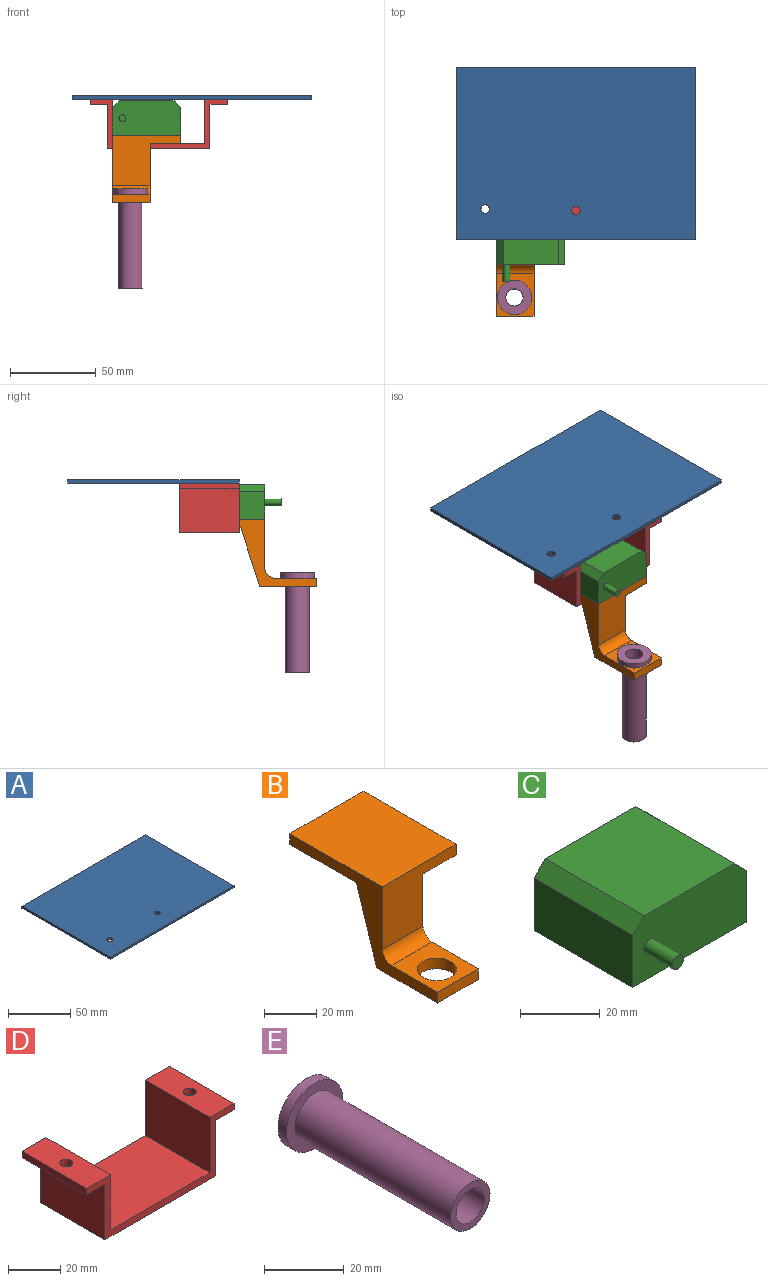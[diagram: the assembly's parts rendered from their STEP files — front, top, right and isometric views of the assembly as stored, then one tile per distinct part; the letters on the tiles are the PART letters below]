
ASSEMBLY  parts=5 mates=12
PART A: 8 faces, bbox 140x100x2 mm
  f0: plane 140x100mm, normal (0,0,1), area 13960.7mm2, adj f1,f3,f4,f5,f6,f7
  f1: plane 100x2mm, normal (-1,0,0), area 200mm2, adj f0,f2,f4,f5
  f2: plane 140x100mm, normal (0,0,-1), area 13960.7mm2, adj f1,f3,f4,f5,f6,f7
  f3: plane 100x2mm, normal (1,0,0), area 200mm2, adj f0,f2,f4,f5
  f4: plane 140x2mm, normal (0,-1,0), area 280mm2, adj f0,f1,f2,f3
  f5: plane 140x2mm, normal (0,1,0), area 280mm2, adj f0,f1,f2,f3
  f6: cylinder r=2.5mm len=5mm, axis (0,0,1), area 31.4mm2, adj f0,f2
  f7: cylinder r=2.5mm len=5mm, axis (0,0,1), area 31.4mm2, adj f0,f2
PART B: 13 faces, bbox 40x80x39.4 mm
  f0: plane 25x22mm, normal (0,0,1), area 373.3mm2, adj f4,f9,f10,f11,f12
  f1: plane 40x29.4mm, normal (0,-1,0), area 736.8mm2, adj f2,f3,f4,f5,f11,f12
  f2: plane 50x40mm, normal (0,0,-1), area 1692mm2, adj f1,f4,f5,f6,f8,f11
  f3: plane 50x40mm, normal (0,0,1), area 2000mm2, adj f1,f4,f5,f6
  f4: plane 80x39.4mm, normal (-1,0,0), area 699.4mm2, adj f0,f1,f2,f3,f6,f7,f8,f9
  f5: plane 50x5mm, normal (1,0,0), area 250mm2, adj f1,f2,f3,f6
  f6: plane 40x5mm, normal (0,1,0), area 200mm2, adj f2,f3,f4,f5
  f7: plane 33x22mm, normal (0,0,-1), area 549.3mm2, adj f4,f8,f9,f10,f11
  f8: plane 34.4x22mm, normal (0,0.95,-0.3), area 794.6mm2, adj f2,f4,f7,f11
  f9: plane 22x5mm, normal (0,-1,0), area 110mm2, adj f0,f4,f7,f11
  f10: cylinder r=7.5mm len=15mm, axis (0,0,1), area 235.6mm2, adj f0,f7
  f11: plane 44x34.4mm, normal (1,0,0), area 449.4mm2, adj f0,f1,f2,f7,f8,f9,f12
  f12: cylinder r=6mm len=22mm, axis (1,0,0), area 166.4mm2, adj f0,f1,f4,f11
PART C: 10 faces, bbox 40x45x20 mm
  f0: plane 35x32mm, normal (0,0,1), area 1120mm2, adj f3,f5,f8,f9
  f1: plane 35x16mm, normal (-1,0,0), area 560mm2, adj f3,f4,f5,f8
  f2: plane 35x16mm, normal (1,0,0), area 560mm2, adj f3,f4,f5,f9
  f3: plane 40x20mm, normal (0,-1,0), area 771.4mm2, adj f0,f1,f2,f4,f6,f8,f9
  f4: plane 40x35mm, normal (0,0,-1), area 1400mm2, adj f1,f2,f3,f5
  f5: plane 40x20mm, normal (0,1,0), area 784mm2, adj f0,f1,f2,f4,f8,f9
  f6: cylinder r=2mm len=10mm, axis (0,1,0), area 125.7mm2, adj f3,f7
  f7: plane 4x4mm, normal (0,-1,0), area 12.6mm2, adj f6
  f8: plane 35x4mm, normal (-0.71,0,0.71), area 198mm2, adj f0,f1,f3,f5
  f9: plane 35x4mm, normal (0.71,0,0.71), area 198mm2, adj f0,f2,f3,f5
PART D: 16 faces, bbox 80x35x29 mm
  f0: plane 35x13mm, normal (0,0,1), area 435.4mm2, adj f1,f11,f12,f13,f15
  f1: plane 35x3mm, normal (-1,0,0), area 105mm2, adj f0,f2,f12,f13
  f2: plane 35x10mm, normal (0,0,-1), area 330.4mm2, adj f1,f3,f12,f13,f15
  f3: plane 35x26mm, normal (-1,0,0), area 910mm2, adj f2,f4,f12,f13
  f4: plane 60x35mm, normal (0,0,-1), area 2100mm2, adj f3,f5,f12,f13
  f5: plane 35x26mm, normal (1,0,0), area 910mm2, adj f4,f6,f12,f13
  f6: plane 35x10mm, normal (0,0,-1), area 330.4mm2, adj f5,f7,f12,f13,f14
  f7: plane 35x3mm, normal (1,0,0), area 105mm2, adj f6,f8,f12,f13
  f8: plane 35x13mm, normal (0,0,1), area 435.4mm2, adj f7,f9,f12,f13,f14
  f9: plane 35x26mm, normal (-1,0,0), area 910mm2, adj f8,f10,f12,f13
  f10: plane 54x35mm, normal (0,0,1), area 1890mm2, adj f9,f11,f12,f13
  f11: plane 35x26mm, normal (1,0,0), area 910mm2, adj f0,f10,f12,f13
  f12: plane 80x29mm, normal (0,-1,0), area 396mm2, adj f0,f1,f2,f3,f4,f5,f6,f7
  f13: plane 80x29mm, normal (0,1,0), area 396mm2, adj f0,f1,f2,f3,f4,f5,f6,f7
  f14: cylinder r=2.5mm len=5mm, axis (0,0,1), area 47.1mm2, adj f6,f8
  f15: cylinder r=2.5mm len=5mm, axis (0,0,1), area 47.1mm2, adj f0,f2
PART E: 6 faces, bbox 20x58x20 mm
  f0: cylinder r=10mm len=20mm, axis (0,1,0), area 188.5mm2, adj f1,f2
  f1: plane 20x20mm, normal (0,-1,0), area 160.2mm2, adj f0,f4
  f2: plane 20x20mm, normal (0,1,0), area 235.6mm2, adj f0,f3
  f3: cylinder r=5mm len=58mm, axis (0,1,0), area 1822.1mm2, adj f2,f5
  f4: cylinder r=7mm len=55mm, axis (0,1,0), area 2419mm2, adj f1,f5
  f5: plane 14x14mm, normal (0,-1,0), area 75.4mm2, adj f3,f4
PLACE A t=(-16.13,59.67,-7.33)mm
PLACE B t=(-69.02,-5.33,-35.69)mm
PLACE C t=(-44.04,-20.33,-24.85)mm
PLACE D t=(-56.02,-5.33,-37.27)mm
PLACE E rot(axis=(0.58,0.58,0.58),120deg) t=(-60.04,-74.33,-61.13)mm
MATE planar D.f9 <-> B.f5  axis (-1,0,0) through (-16.64,-22.83,-21.73)mm
MATE cylindrical D.f15 <-> A.f7  axis (0,0,1) through (-77.14,-22.83,-10.23)mm
MATE planar C.f1 <-> D.f11  axis (-1,0,0) through (-70.64,-37.83,-21.73)mm
MATE planar B.f2 <-> D.f10  axis (0,0,-1) through (-49.01,-27.06,-34.73)mm
MATE planar D.f14 <-> A.f2  axis (0,0,1) through (-10.14,-22.83,-8.73)mm
MATE planar E.f0 <-> B.f0  axis (0,0,-1) through (-60.04,-74.33,-64.13)mm
MATE cylindrical E.f4 <-> B.f10  axis (0,0,1) through (-60.04,-74.33,-91.63)mm
MATE parallel D.f10 <-> B.f2  axis (0,0,1) through (-16.64,-22.83,-34.73)mm
MATE planar C.f4 <-> B.f3  axis (0,0,-1) through (-50.64,-37.83,-29.73)mm
MATE parallel B.f4 <-> D.f11  axis (-1,0,0) through (-70.64,-47.6,-46.6)mm
MATE planar B.f6 <-> D.f13  axis (0,1,0) through (-50.64,-5.33,-32.23)mm
MATE planar C.f3 <-> B.f1  axis (0,-1,0) through (-50.41,-55.33,-19.91)mm
